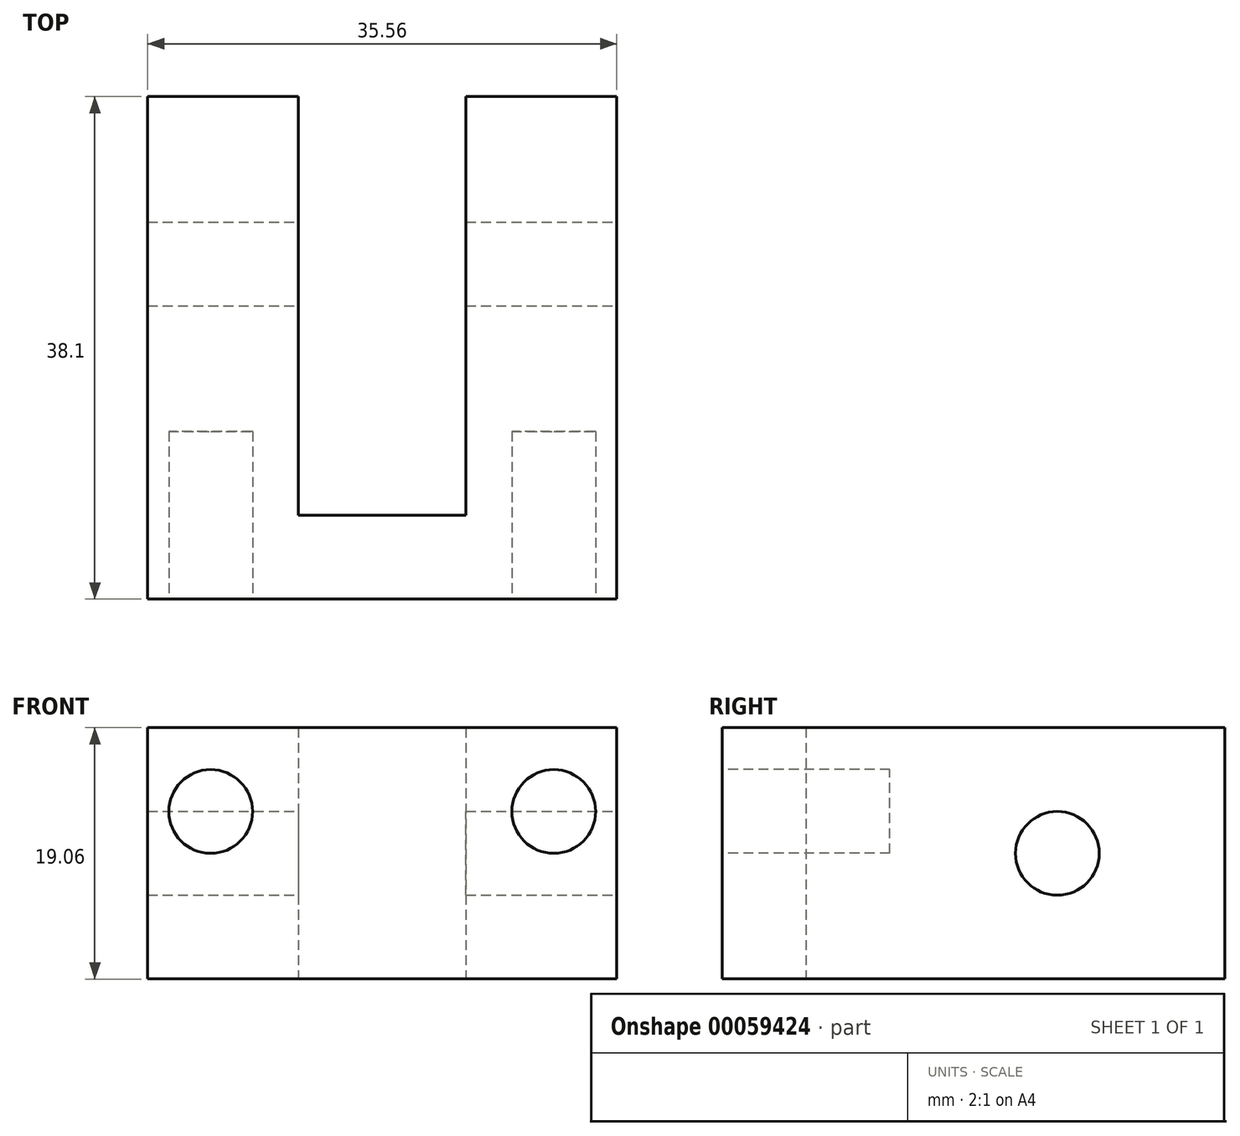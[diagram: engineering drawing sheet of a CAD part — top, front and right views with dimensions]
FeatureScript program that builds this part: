
annotation { "Feature Type Name" : "Feature", "Feature Type Description" : "" }
export const myFeature = defineFeature(function(context is Context, id is Id, definition is map)
    precondition{}
    {
        {
            var Q0;
            Q0=qCreatedBy(makeId("Top.planeOp"),FACE);
            var sketch = newSketch(context, id + "F0", { "sketchPlane" : qUnion([Q0])});
            skLineSegment(sketch, "E0", {"start": v(-17.78, 0) * mm, "end": v(17.78, 0) * mm});
            skLineSegment(sketch, "E1", {"start": v(17.78, 0) * mm, "end": v(17.78, 38.1) * mm});
            skLineSegment(sketch, "E2", {"start": v(17.78, 38.1) * mm, "end": v(6.35, 38.1) * mm});
            skLineSegment(sketch, "E3", {"start": v(6.35, 38.1) * mm, "end": v(6.35, 6.35) * mm});
            skLineSegment(sketch, "E4", {"start": v(6.35, 6.35) * mm, "end": v(-6.35, 6.35) * mm});
            skLineSegment(sketch, "E5", {"start": v(-6.35, 6.35) * mm, "end": v(-6.35, 38.1) * mm});
            skLineSegment(sketch, "E6", {"start": v(-6.35, 38.1) * mm, "end": v(-17.78, 38.1) * mm});
            skLineSegment(sketch, "E7", {"start": v(-17.78, 0) * mm, "end": v(-17.78, 38.1) * mm});
            skSolve(sketch);
        }
        {
            var Q0;
            Q0 = qSketchRegion(id + "F0", true);
            extrude(context, id + "F1", {"entities" : qUnion([Q0]), "endBound" : BoundingType.SYMMETRIC, "depth" : 19.05 * mm});
        }
        {
            var Q0;
            Q0=makeQuery(id+"F1.opExtrude","SWEPT_FACE",FACE,{"disambiguationData":[OSD([sQuery(id+"F0.wireOp",EDGE,"E0")])]});
            var sketch = newSketch(context, id + "F2", { "sketchPlane" : qUnion([Q0])});
            skCircle(sketch, "E8", {"center": v(-13, 3.18) * mm, "radius": 3.18 * mm});
            skCircle(sketch, "E9", {"center": v(13, 3.18) * mm, "radius": 3.18 * mm});
            skSolve(sketch);
        }
        {
            var Q0;
            Q0=makeQuery(id+"F2.imprint","IMPRINT",FACE,{"disambiguationData":[TD([[makeQuery(id+"F2.imprint","IMPRINT",EDGE,{"derivedFrom":sQuery(id+"F2.wireOp",EDGE,"E8")}),1.0]])]});
            var Q1;
            Q1=makeQuery(id+"F2.imprint","IMPRINT",FACE,{"disambiguationData":[TD([[makeQuery(id+"F2.imprint","IMPRINT",EDGE,{"derivedFrom":sQuery(id+"F2.wireOp",EDGE,"E9")}),1.0]])]});
            extrude(context, id + "F3", {"entities" : qUnion([Q0, Q1]), "operationType" : NewBodyOperationType.REMOVE, "oppositeDirection" : true, "depth" : 12.7 * mm});
        }
        {
            var Q0;
            Q0=makeQuery(id+"F1.opExtrude","SWEPT_FACE",FACE,{"disambiguationData":[OSD([sQuery(id+"F0.wireOp",EDGE,"E1")])]});
            var sketch = newSketch(context, id + "F4", { "sketchPlane" : qUnion([Q0])});
            skCircle(sketch, "E10", {"center": v(25.4, 0) * mm, "radius": 3.18 * mm});
            skSolve(sketch);
        }
        {
            var Q0;
            Q0 = qSketchRegion(id + "F4", true);
            extrude(context, id + "F5", {"entities" : qUnion([Q0]), "operationType" : NewBodyOperationType.REMOVE, "endBound" : BoundingType.THROUGH_ALL, "oppositeDirection" : true, "depth" : 43.8 * mm});
        }
    });
